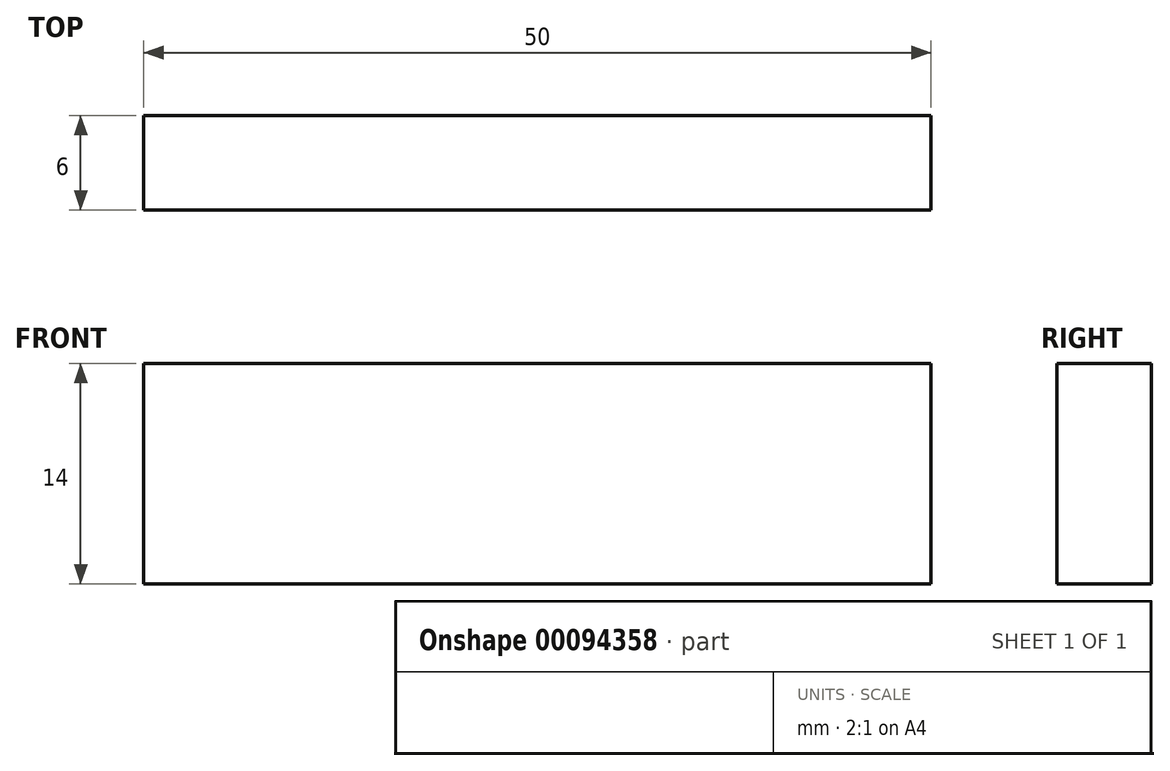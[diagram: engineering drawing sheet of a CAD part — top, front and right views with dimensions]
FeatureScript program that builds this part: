
annotation { "Feature Type Name" : "Feature", "Feature Type Description" : "" }
export const myFeature = defineFeature(function(context is Context, id is Id, definition is map)
    precondition{}
    {
        {
            var Q0;
            Q0=qCreatedBy(makeId("Top.planeOp"),FACE);
            var sketch = newSketch(context, id + "F0", { "sketchPlane" : qUnion([Q0])});
            skLineSegment(sketch, "E0.bottom", {"start": v(25, -3) * mm, "end": v(-25, -3) * mm});
            skLineSegment(sketch, "E0.top", {"start": v(25, 3) * mm, "end": v(-25, 3) * mm});
            skLineSegment(sketch, "E0.left", {"start": v(25, -3) * mm, "end": v(25, 3) * mm});
            skLineSegment(sketch, "E0.right", {"start": v(-25, -3) * mm, "end": v(-25, 3) * mm});
            skPoint(sketch, "E0.middle", {"position": v(0, 0) * mm});
            skSolve(sketch);
        }
        {
            var Q0;
            Q0=makeQuery(id+"F0.imprint","IMPRINT",FACE,{"disambiguationData":[TD([[makeQuery(id+"F0.imprint","IMPRINT",EDGE,{"derivedFrom":sQuery(id+"F0.wireOp",EDGE,"E0.bottom")}),-1.0]])]});
            extrude(context, id + "F1", {"entities" : qUnion([Q0]), "depth" : 14 * mm, "offsetDistance" : 25 * mm});
        }
    });
